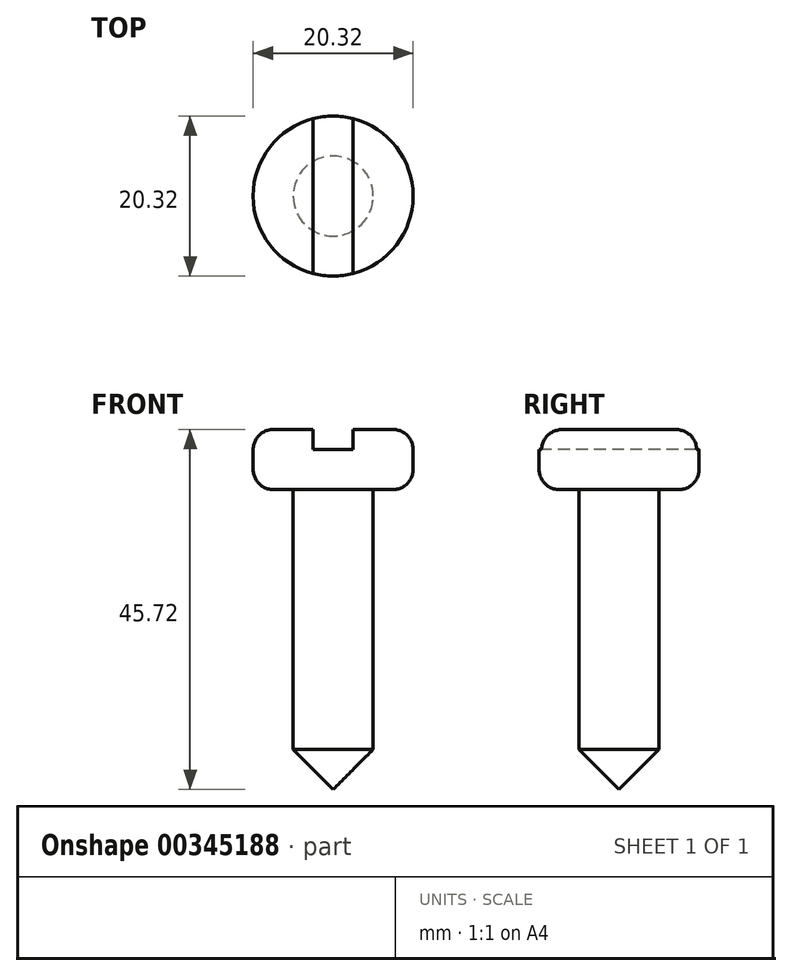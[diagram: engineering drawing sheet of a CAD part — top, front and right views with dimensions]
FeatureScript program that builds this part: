
annotation { "Feature Type Name" : "Feature", "Feature Type Description" : "" }
export const myFeature = defineFeature(function(context is Context, id is Id, definition is map)
    precondition{}
    {
        {
            var Q0;
            Q0=qCreatedBy(makeId("Front.planeOp"),FACE);
            var sketch = newSketch(context, id + "F0", { "sketchPlane" : qUnion([Q0])});
            skLineSegment(sketch, "E0", {"start": v(0, 0) * mm, "end": v(0, 45.72) * mm});
            skLineSegment(sketch, "E1", {"start": v(0, 45.72) * mm, "end": v(10.16, 45.72) * mm});
            skLineSegment(sketch, "E2", {"start": v(10.16, 45.72) * mm, "end": v(10.16, 38.1) * mm});
            skLineSegment(sketch, "E3", {"start": v(10.16, 38.1) * mm, "end": v(5.08, 38.1) * mm});
            skLineSegment(sketch, "E4", {"start": v(5.08, 38.1) * mm, "end": v(5.08, 5.08) * mm});
            skLineSegment(sketch, "E5", {"start": v(5.08, 5.08) * mm, "end": v(0, 0) * mm});
            skSolve(sketch);
        }
        {
            var Q0;
            Q0=makeQuery(id+"F0.imprint","IMPRINT",FACE,{"disambiguationData":[TD([[makeQuery(id+"F0.imprint","IMPRINT",EDGE,{"derivedFrom":sQuery(id+"F0.wireOp",EDGE,"E0")}),-1.0]])]});
            var Q1;
            Q1=sQuery(id+"F0.wireOp",EDGE,"E0");
            revolve(context, id + "F1", {"entities" : qUnion([Q0]), "axis" : qUnion([Q1]), "revolveType" : RevolveType.FULL});
        }
        {
            var Q0;
            Q0=makeQuery(id+"F1.opRevolve","SWEPT_EDGE",EDGE,{"disambiguationData":[OSD([sQuery(id+"F0.wireOp",EDGE,"E1"),sQuery(id+"F0.wireOp",EDGE,"E2")])]});
            var Q1;
            Q1=makeQuery(id+"F1.opRevolve","SWEPT_EDGE",EDGE,{"disambiguationData":[OSD([sQuery(id+"F0.wireOp",EDGE,"E2"),sQuery(id+"F0.wireOp",EDGE,"E3")])]});
            fillet(context, id + "F2", {"entities" : qUnion([Q0, Q1]), "radius" : 2.54 * mm, "tangentPropagation" : true, "allowEdgeOverflow" : false});
        }
        {
            var Q0;
            Q0=makeQuery(id+"F1.opRevolve","SWEPT_FACE",FACE,{"disambiguationData":[OSD([sQuery(id+"F0.wireOp",EDGE,"E1")])]});
            var sketch = newSketch(context, id + "F3", { "sketchPlane" : qUnion([Q0])});
            skLineSegment(sketch, "E6.bottom", {"start": v(-2.54, 10.9) * mm, "end": v(2.54, 10.9) * mm});
            skLineSegment(sketch, "E6.top", {"start": v(-2.54, -11.18) * mm, "end": v(2.54, -11.18) * mm});
            skLineSegment(sketch, "E6.left", {"start": v(-2.54, 10.9) * mm, "end": v(-2.54, -11.18) * mm});
            skLineSegment(sketch, "E6.right", {"start": v(2.54, 10.9) * mm, "end": v(2.54, -11.18) * mm});
            skSolve(sketch);
        }
        {
            var Q0;
            Q0 = qSketchRegion(id + "F3", true);
            extrude(context, id + "F4", {"entities" : qUnion([Q0]), "operationType" : NewBodyOperationType.REMOVE, "oppositeDirection" : true, "depth" : 2.54 * mm});
        }
    });
